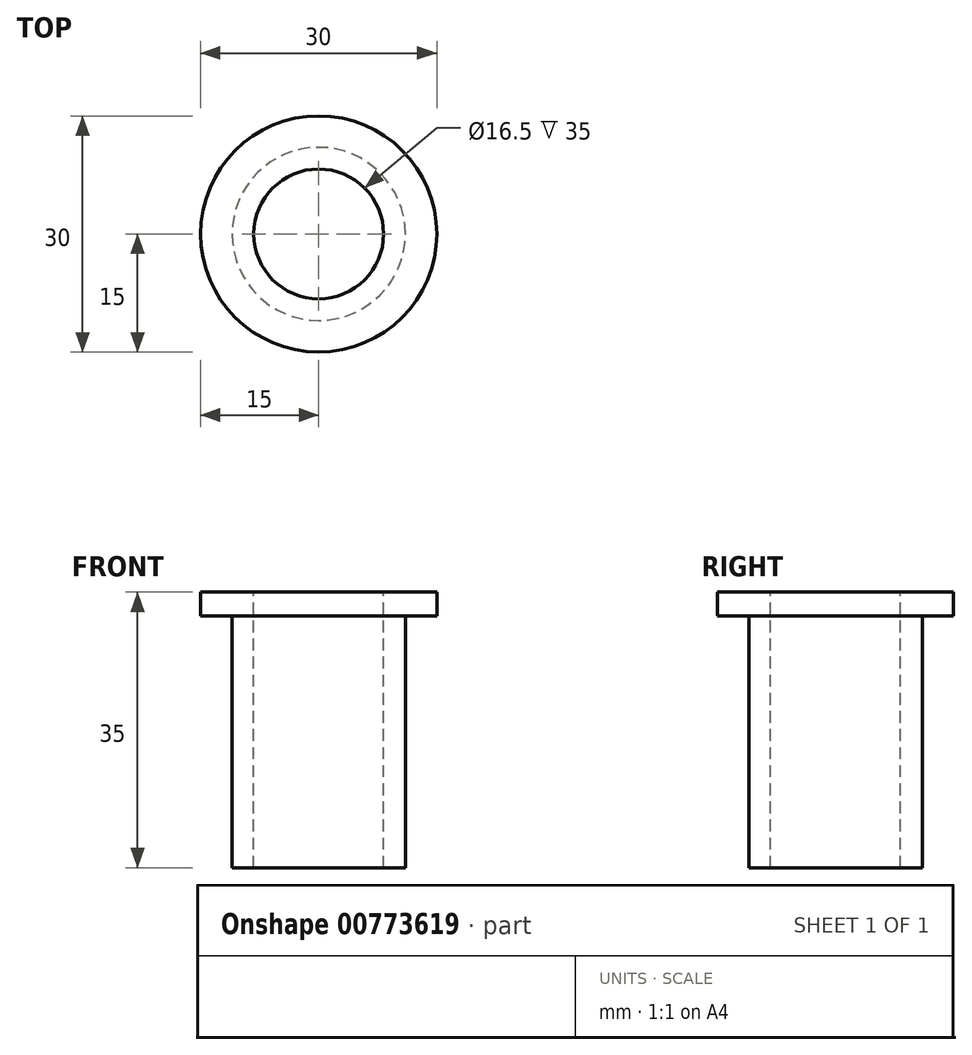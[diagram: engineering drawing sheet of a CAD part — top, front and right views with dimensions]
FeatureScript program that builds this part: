
annotation { "Feature Type Name" : "Feature", "Feature Type Description" : "" }
export const myFeature = defineFeature(function(context is Context, id is Id, definition is map)
    precondition{}
    {
        {
            var Q0;
            Q0=qCreatedBy(makeId("Top.planeOp"),FACE);
            var sketch = newSketch(context, id + "F0", { "sketchPlane" : qUnion([Q0])});
            skCircle(sketch, "E0", {"center": v(0, 0) * mm, "radius": 8.25 * mm});
            skCircle(sketch, "E1", {"center": v(0, 0) * mm, "radius": 11 * mm});
            skCircle(sketch, "E2", {"center": v(0, 0) * mm, "radius": 15 * mm});
            skSolve(sketch);
        }
        {
            var Q0;
            Q0=makeQuery(id+"F0.imprint","IMPRINT",FACE,{"disambiguationData":[TD([[makeQuery(id+"F0.imprint","IMPRINT",EDGE,{"derivedFrom":sQuery(id+"F0.wireOp",EDGE,"E0")}),-1.0]])]});
            extrude(context, id + "F1", {"entities" : qUnion([Q0]), "oppositeDirection" : true, "depth" : 32 * mm, "offsetDistance" : 25 * mm});
        }
        {
            var Q0;
            Q0=makeQuery(id+"F0.imprint","IMPRINT",FACE,{"disambiguationData":[TD([[makeQuery(id+"F0.imprint","IMPRINT",EDGE,{"derivedFrom":sQuery(id+"F0.wireOp",EDGE,"E1")}),-1.0]])]});
            var Q1;
            Q1=makeQuery(id+"F0.imprint","IMPRINT",FACE,{"disambiguationData":[TD([[makeQuery(id+"F0.imprint","IMPRINT",EDGE,{"derivedFrom":sQuery(id+"F0.wireOp",EDGE,"E0")}),-1.0]])]});
            extrude(context, id + "F2", {"entities" : qUnion([Q0, Q1]), "operationType" : NewBodyOperationType.ADD, "depth" : 3 * mm, "offsetDistance" : 25 * mm});
        }
    });
